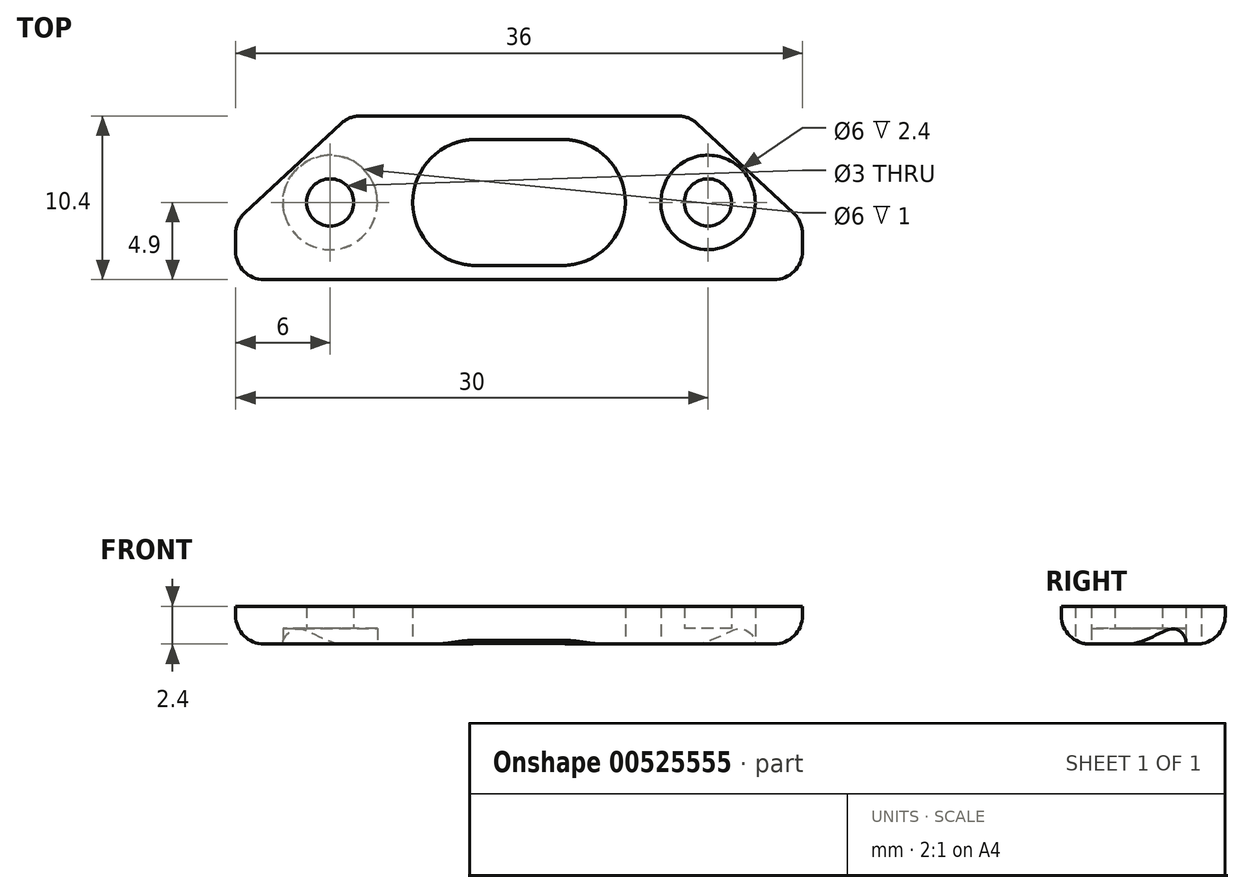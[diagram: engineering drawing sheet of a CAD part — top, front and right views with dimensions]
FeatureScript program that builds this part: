
annotation { "Feature Type Name" : "Feature", "Feature Type Description" : "" }
export const myFeature = defineFeature(function(context is Context, id is Id, definition is map)
    precondition{}
    {
        {
            var Q0;
            Q0=qCreatedBy(makeId("Top.planeOp"),FACE);
            var sketch = newSketch(context, id + "F0", { "sketchPlane" : qUnion([Q0])});
            skLineSegment(sketch, "E0.bottom", {"start": v(-18, -4.9) * mm, "end": v(18, -4.9) * mm});
            skLineSegment(sketch, "E0.top", {"start": v(-10.78, 5.5) * mm, "end": v(10.78, 5.5) * mm});
            skLineSegment(sketch, "E0.left", {"start": v(-18, -4.9) * mm, "end": v(-18, -1.2) * mm});
            skLineSegment(sketch, "E0.right", {"start": v(18, -4.9) * mm, "end": v(18, -1.2) * mm});
            skCircle(sketch, "E1", {"center": v(-12, 0) * mm, "radius": 1.5 * mm});
            skCircle(sketch, "E2.MirrorC", {"center": v(12, 0) * mm, "radius": 1.5 * mm});
            skCircle(sketch, "E3", {"center": v(-12, 0) * mm, "radius": 3 * mm});
            skCircle(sketch, "E4.MirrorC", {"center": v(12, 0) * mm, "radius": 3 * mm});
            skArc(sketch, "E5", {"start": v(-2.75, 4) * mm, "mid": v(-6.75, 0) * mm, "end": v(-2.75, -4) * mm});
            skArc(sketch, "E6", {"start": v(2.75, -4) * mm, "mid": v(6.75, 0) * mm, "end": v(2.75, 4) * mm});
            skLineSegment(sketch, "E7", {"start": v(-2.75, 4) * mm, "end": v(2.75, 4) * mm});
            skLineSegment(sketch, "E8", {"start": v(-2.75, -4) * mm, "end": v(2.75, -4) * mm});
            skLineSegment(sketch, "E9", {"start": v(18, -1.2) * mm, "end": v(10.78, 5.5) * mm});
            skLineSegment(sketch, "E10.MirrorCS", {"start": v(-18, -1.2) * mm, "end": v(-10.78, 5.5) * mm});
            skPoint(sketch, "E11.center.orphan", {"position": v(-15.26, 6.06) * mm});
            skSolve(sketch);
        }
        {
            var Q0;
            Q0 = qSketchRegion(id + "F0", true);
            var Q1;
            Q1=makeQuery(id+"F0.imprint","IMPRINT",FACE,{"disambiguationData":[TD([[makeQuery(id+"F0.imprint","IMPRINT",EDGE,{"derivedFrom":sQuery(id+"F0.wireOp",EDGE,"E1")}),-1.0]])]});
            var Q2;
            Q2=makeQuery(id+"F0.imprint","IMPRINT",FACE,{"disambiguationData":[TD([[makeQuery(id+"F0.imprint","IMPRINT",EDGE,{"derivedFrom":sQuery(id+"F0.wireOp",EDGE,"E2.MirrorC")}),1.0]])]});
            extrude(context, id + "F1", {"entities" : qUnion([Q0, Q1, Q2]), "depth" : 2.4 * mm, "offsetDistance" : 25 * mm});
        }
        {
            var Q0;
            Q0=makeQuery(id+"F0.imprint","IMPRINT",FACE,{"disambiguationData":[TD([[makeQuery(id+"F0.imprint","IMPRINT",EDGE,{"derivedFrom":sQuery(id+"F0.wireOp",EDGE,"E2.MirrorC")}),1.0]])]});
            var Q1;
            Q1=makeQuery(id+"F0.imprint","IMPRINT",FACE,{"disambiguationData":[TD([[makeQuery(id+"F0.imprint","IMPRINT",EDGE,{"derivedFrom":sQuery(id+"F0.wireOp",EDGE,"E1")}),-1.0]])]});
            extrude(context, id + "F2", {"entities" : qUnion([Q0, Q1]), "operationType" : NewBodyOperationType.REMOVE, "depth" : 1 * mm, "offsetDistance" : 25 * mm});
        }
        {
            var Q0;
            Q0=makeQuery(id+"F1.opExtrude","CAP_EDGE",EDGE,{"disambiguationData":[OSD([sQuery(id+"F0.wireOp",EDGE,"E0.left")])],"isStart":true});
            var Q1;
            Q1=makeQuery(id+"F1.opExtrude","CAP_EDGE",EDGE,{"disambiguationData":[OSD([sQuery(id+"F0.wireOp",EDGE,"E0.bottom")])],"isStart":true});
            var Q2;
            Q2=makeQuery(id+"F1.opExtrude","CAP_EDGE",EDGE,{"disambiguationData":[OSD([sQuery(id+"F0.wireOp",EDGE,"E0.right")])],"isStart":true});
            var Q3;
            Q3=makeQuery(id+"F1.opExtrude","CAP_EDGE",EDGE,{"disambiguationData":[OSD([sQuery(id+"F0.wireOp",EDGE,"E0.top")])],"isStart":true});
            var Q4;
            Q4=makeQuery(id+"F1.opExtrude","SWEPT_EDGE",EDGE,{"disambiguationData":[OSD([sQuery(id+"F0.wireOp",EDGE,"E0.top"),sQuery(id+"F0.wireOp",EDGE,"E9")])]});
            var Q5;
            Q5=makeQuery(id+"F1.opExtrude","CAP_EDGE",EDGE,{"disambiguationData":[OSD([sQuery(id+"F0.wireOp",EDGE,"E10.MirrorCS")])],"isStart":true});
            var Q6;
            Q6=makeQuery(id+"F1.opExtrude","CAP_EDGE",EDGE,{"disambiguationData":[OSD([sQuery(id+"F0.wireOp",EDGE,"E9")])],"isStart":true});
            var Q7;
            Q7=makeQuery(id+"F1.opExtrude","SWEPT_EDGE",EDGE,{"disambiguationData":[OSD([sQuery(id+"F0.wireOp",EDGE,"E0.bottom"),sQuery(id+"F0.wireOp",EDGE,"E0.left")])]});
            var Q8;
            Q8=makeQuery(id+"F1.opExtrude","SWEPT_EDGE",EDGE,{"disambiguationData":[OSD([sQuery(id+"F0.wireOp",EDGE,"E0.bottom"),sQuery(id+"F0.wireOp",EDGE,"E0.right")])]});
            var Q9;
            Q9=makeQuery(id+"F1.opExtrude","SWEPT_EDGE",EDGE,{"disambiguationData":[OSD([sQuery(id+"F0.wireOp",EDGE,"E0.left"),sQuery(id+"F0.wireOp",EDGE,"E10.MirrorCS")])]});
            var Q10;
            Q10=makeQuery(id+"F1.opExtrude","SWEPT_EDGE",EDGE,{"disambiguationData":[OSD([sQuery(id+"F0.wireOp",EDGE,"E0.right"),sQuery(id+"F0.wireOp",EDGE,"E9")])]});
            var Q11;
            Q11=makeQuery(id+"F1.opExtrude","SWEPT_EDGE",EDGE,{"disambiguationData":[OSD([sQuery(id+"F0.wireOp",EDGE,"E0.top"),sQuery(id+"F0.wireOp",EDGE,"E10.MirrorCS")])]});
            fillet(context, id + "F3", {"entities" : qUnion([Q0, Q1, Q2, Q3, Q4, Q5, Q6, Q7, Q8, Q9, Q10, Q11]), "radius" : 1.8 * mm, "tangentPropagation" : true, "allowEdgeOverflow" : false});
        }
    });
